# Revit family: Kitchen_Sinks_AXOR_42818XXX-AXOR-Uno-Liquid-soap111r
name_source: partatom
category: Furniture
revit_build: Autodesk Revit 2018 (Build: 20170223_1515(x64)
units: mm (PartAtom-declared; Revit-internal decimal feet)

## family parameters
Always vertical = No
Cut with Voids When Loaded = No
OmniClass Number = 23.31.25.29.13
OmniClass Title = Hand Soap Dispensers
Room Calculation Point = No
Shared = No
Work Plane-Based = Yes

## types (5) — shared parameters
Always visible = Yes
BIMobject category = Accessories
Default Elevation = 1219.2 mm  [stored 4 ft]
Description = AXOR Uno Liquid soap dispenser/ washing-up liquid dispenser
Design country = Germany
EAN code = 4059625428559
Edition number = 1
GTIN code = https://4059625428559
IFC Classification = Furnishing Element
Manufacturer = AXOR
Manufacturer country = Germany
Manufacturer name = AXOR
Material main = Metal
Material secondary = Chrome
Model = 42818XXX
OmniClass Code = 23-31 25 29 13
OmniClass Description = Hand Soap Dispensers
Product Guid = 0803d9df-c782-4aae-9133-988636cf04a3
Product SKU = 42818XXX
Product data url = https://bimobject.com
Product family = AXOR Uno
Product group = Sink accessoires
Product name = 42818XXX AXOR Uno Liquid soap dispenser/ washing-up liquid dispenser
QR code = https://bimobject.com
URL = https://www.axor-design.com
Weight Net (Kg) = 395

## per-type parameters (varying)
| type | Material 1 |
| 800 Stainless Steel Optic | AXOR - Metal - 800 Stainless Steel Optic |
| 670 Matt Black | AXOR - Metal - 670 Matt Black |
| 340 Brushed Black Chrome | AXOR - Metal - 340 Brushed Black Chrome |
| 330 Polished Black Chrome | AXOR - Metal - 330 Polished Black Chrome |
| 000 Chrome | AXOR - Metal - 000 Chrome |

note: [stored X ft] marks values corroborated as IEEE doubles in the binary element streams (Revit-internal decimal feet)

## geometry (parser evidence)
native form markers: Sweep x1
no freeform markers — native parametric forms only
